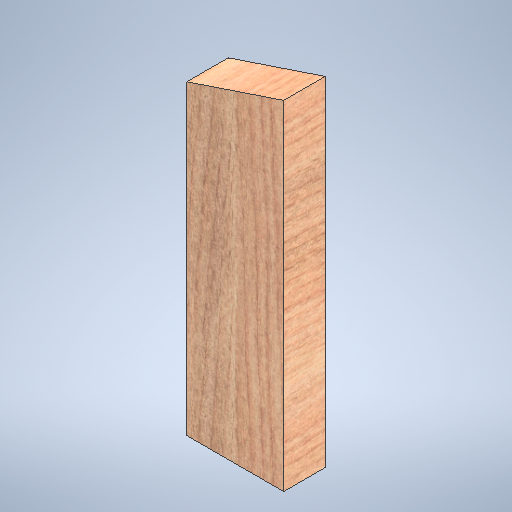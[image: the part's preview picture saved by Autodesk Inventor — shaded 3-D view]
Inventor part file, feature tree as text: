
AUTODESK INVENTOR PART (.ipt)
format: ipt  version: 2025.1 (Build 291241020, 241B)  size: 402,432 bytes
history: native  units: in
note: dims shown in document units (in); Inventor stores cm internally (conversion verified against a paired STEP export)
features: extrude x1, sketch x1
ambient origin geometry x8: Origin, YZ Plane, XZ Plane, XY Plane, X Axis, Y Axis, Z Axis, Center Point
bodies: Solid1 (feature_tree)
feature tree (2):
  extrude  "Extrusion1"  Depth=1.5in TaperAngle=0.0deg
  sketch  "Sketch1"  dims[d3=3.5in d4=1.5in d5=0.0in d6=12.2372in d9=128.5in d10=42.875in]
